# Revit family: L300xH200
name_source: partatom
category: Duct Accessories
revit_build: Autodesk Revit 2018 (Build: 20170223_1515(x64)
units: mm (PartAtom-declared; Revit-internal decimal feet)

## family parameters
Always vertical = Yes
Cut with Voids When Loaded = No
OmniClass Number = 23.75.70.11.14.14
OmniClass Title = Dampers for Air Ductwork
Part Type = Damper
Round Connector Dimension = Use Diameter
Shared = No
Work Plane-Based = No

## types (1)
- GRYFIT NEO-V, LxH=300x200, Galvanized steel, KP 20 + EMS + SDG-15-24 + TKA, L=300. H=200
    Actuator type. = SDG-15
    Actuator voltage. = 24/48 V AC/DC
    Colour of grille. = ocynk.
    Connector. = rectangular flange connector 20 mm
    Damper Length = 150 mm
    Damper Material = <By Category>
    Damper external height (H1). = 240
    Damper external width (L1). = 505
    Dimensions as 5 mm in the standard. = No
    Double Beginning and End (2WKKP) = None
    EMS module = Yes
    Electromagnet = No
    Fire resistance class. = EI120 (vew-i↔o) S1500 C10000 AA multi
    Geometry = GRYFIT NEO-V, LxH=300x200, Galvanized steel, KP 20 + EMS + SDG-15-24 + TKA, L=300. H=200
    Grille external height (Hg). = 240
    Grille external width (Lg). = 505
    HMG gaskets = No
    Half Damper Length = 75 mm
    Height (H). = 160
    Height of installation opening (Hr). = 290
    Installation brackets = No
    Length (P). = 120
    Material of damper. = Galvanized steel
    Material of grille. = Galvanized steel
    Protective grille (TRA) = Protective grille (TKA)
    Type. = GRYFIT NEO-V
    Width (L). = 465
    Width as 5mm (L 5mm). = 600
    Width of installation opening (Lr). = 555
    Without cable glands = No
    anglXY1 = 180.00°
    anglZ1 = 0.00°
    heightcon1 = 200 mm
    lengX1 = 0 mm  [stored 0 ft]
    lengXY1 = 600 mm
    lengXYZ1 = 500 mm  [stored 1.64042 ft]
    lengY1 = 83 mm
    lengZ1 = 0 mm  [stored 0 ft]
    rotcon1 = 0 mm
    widthcon1 = 300 mm

note: [stored X ft] marks values corroborated as IEEE doubles in the binary element streams (Revit-internal decimal feet)

## geometry (parser evidence)
native form markers: Sweep x4
no freeform markers — native parametric forms only
